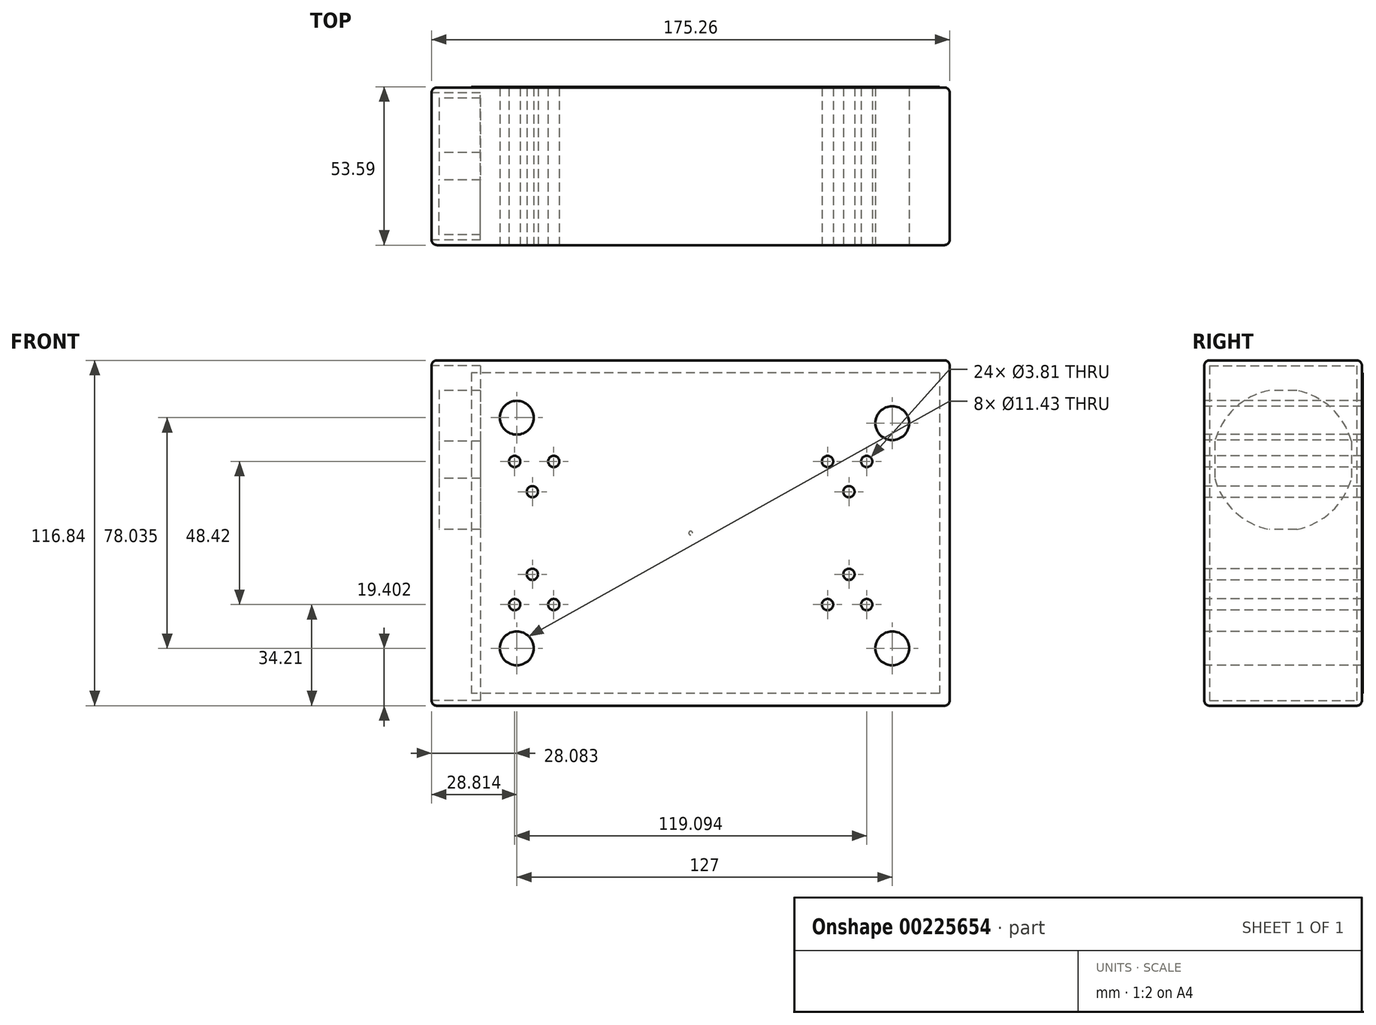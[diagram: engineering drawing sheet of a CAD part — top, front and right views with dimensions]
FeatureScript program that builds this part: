
annotation { "Feature Type Name" : "Feature", "Feature Type Description" : "" }
export const myFeature = defineFeature(function(context is Context, id is Id, definition is map)
    precondition{}
    {
        {
            var Q0;
            Q0=qCreatedBy(makeId("Front.planeOp"),FACE);
            var sketch = newSketch(context, id + "F0", { "sketchPlane" : qUnion([Q0])});
            skLineSegment(sketch, "E0.bottom", {"start": v(-87.63, 58.42) * mm, "end": v(87.63, 58.42) * mm});
            skLineSegment(sketch, "E0.top", {"start": v(-87.63, -58.42) * mm, "end": v(87.63, -58.42) * mm});
            skLineSegment(sketch, "E0.left", {"start": v(-87.63, 58.42) * mm, "end": v(-87.63, -58.42) * mm});
            skLineSegment(sketch, "E0.right", {"start": v(87.63, 58.42) * mm, "end": v(87.63, -58.42) * mm});
            skPoint(sketch, "E0.middle", {"position": v(0, 0) * mm});
            skSolve(sketch);
        }
        {
            var Q0;
            Q0=makeQuery(id+"F0.imprint","IMPRINT",FACE,{"disambiguationData":[TD([[makeQuery(id+"F0.imprint","IMPRINT",EDGE,{"derivedFrom":sQuery(id+"F0.wireOp",EDGE,"E0.bottom")}),-1.0]])]});
            extrude(context, id + "F1", {"entities" : qUnion([Q0]), "depth" : 53.34 * mm});
        }
        {
            var Q0;
            Q0=makeQuery(id+"F1.opExtrude","CAP_FACE",FACE,{"disambiguationData":[OSD([sQuery(id+"F0.wireOp",EDGE,"E0.bottom"),sQuery(id+"F0.wireOp",EDGE,"E0.top"),sQuery(id+"F0.wireOp",EDGE,"E0.left"),sQuery(id+"F0.wireOp",EDGE,"E0.right")])],"isStart":true});
            var sketch = newSketch(context, id + "F2", { "sketchPlane" : qUnion([Q0])});
            skLineSegment(sketch, "E1", {"start": v(-87.63, 54.2) * mm, "end": v(87.63, 54.2) * mm});
            skLineSegment(sketch, "E2.MirrorCS", {"start": v(-87.63, -54.2) * mm, "end": v(87.63, -54.2) * mm});
            skLineSegment(sketch, "E3", {"start": v(74.22, 58.42) * mm, "end": v(74.22, -58.42) * mm});
            skLineSegment(sketch, "E4", {"start": v(-84.2, 54.2) * mm, "end": v(-84.2, -58.42) * mm});
            skCircle(sketch, "E5", {"center": v(0, 0) * mm, "radius": 0.64 * mm});
            skSolve(sketch);
        }
        {
            var Q0;
            Q0 = qSketchRegion(id + "F2", true);
            extrude(context, id + "F3", {"entities" : qUnion([Q0]), "depth" : 0.25 * mm});
        }
        {
            var Q0;
            Q0=makeQuery(id+"F1.opExtrude","CAP_FACE",FACE,{"disambiguationData":[OSD([sQuery(id+"F0.wireOp",EDGE,"E0.bottom"),sQuery(id+"F0.wireOp",EDGE,"E0.top"),sQuery(id+"F0.wireOp",EDGE,"E0.left"),sQuery(id+"F0.wireOp",EDGE,"E0.right")])],"isStart":false});
            var sketch = newSketch(context, id + "F4", { "sketchPlane" : qUnion([Q0])});
            skCircle(sketch, "E6", {"center": v(68.18, -39.02) * mm, "radius": 4.35 * mm});
            skCircle(sketch, "E7", {"center": v(-58.82, -39.02) * mm, "radius": 4.87 * mm});
            skCircle(sketch, "E8", {"center": v(68.18, 37.18) * mm, "radius": 4.37 * mm});
            skCircle(sketch, "E9.MirrorC", {"center": v(-58.82, 39.02) * mm, "radius": 4.87 * mm});
            skCircle(sketch, "E10", {"center": v(59.55, -24.2) * mm, "radius": 1.93 * mm});
            skCircle(sketch, "E11", {"center": v(53.53, -13.98) * mm, "radius": 1.7 * mm});
            skCircle(sketch, "E12", {"center": v(46.31, -24.2) * mm, "radius": 1.93 * mm});
            skCircle(sketch, "E13.MirrorC", {"center": v(59.55, 24.2) * mm, "radius": 1.93 * mm});
            skCircle(sketch, "E14.MirrorC", {"center": v(46.31, 24.2) * mm, "radius": 1.93 * mm});
            skCircle(sketch, "E15.MirrorC", {"center": v(53.53, 13.98) * mm, "radius": 1.7 * mm});
            skCircle(sketch, "E16.MirrorC", {"center": v(-46.31, -24.2) * mm, "radius": 1.93 * mm});
            skCircle(sketch, "E17.MirrorC", {"center": v(-59.55, -24.2) * mm, "radius": 1.93 * mm});
            skCircle(sketch, "E18.MirrorC", {"center": v(-53.53, -13.98) * mm, "radius": 1.7 * mm});
            skCircle(sketch, "E19.MirrorC", {"center": v(-46.31, 24.2) * mm, "radius": 1.93 * mm});
            skCircle(sketch, "E20.MirrorC", {"center": v(-53.53, 13.98) * mm, "radius": 1.7 * mm});
            skCircle(sketch, "E21.MirrorC", {"center": v(-59.55, 24.2) * mm, "radius": 1.93 * mm});
            skSolve(sketch);
        }
        {
            var Q0;
            Q0=sQuery(id+"F4.wireOp",VERTEX,"E6.center");
            var Q1;
            Q1=sQuery(id+"F4.wireOp",VERTEX,"E8.center");
            var Q2;
            Q2=sQuery(id+"F4.wireOp",VERTEX,"E7.center");
            var Q3;
            Q3=sQuery(id+"F4.wireOp",VERTEX,"E9.MirrorC.center");
            var Q4;
            Q4=makeQuery(id+"F1.opExtrude","SWEPT_BODY",BODY,{"disambiguationData":[OSD([sQuery(id+"F0.wireOp",EDGE,"E0.bottom"),sQuery(id+"F0.wireOp",EDGE,"E0.top"),sQuery(id+"F0.wireOp",EDGE,"E0.left"),sQuery(id+"F0.wireOp",EDGE,"E0.right")])]});
            var Q5;
            Q5=makeQuery(id+"F3.opExtrude","SWEPT_BODY",BODY,{"disambiguationData":[OSD([sQuery(id+"F2.wireOp",EDGE,"E1"),sQuery(id+"F2.wireOp",EDGE,"E2.MirrorCS"),sQuery(id+"F2.wireOp",EDGE,"E3"),sQuery(id+"F2.wireOp",EDGE,"E4")])]});
            hole(context, id + "F5", {"style" : HoleStyle.SIMPLE, "endStyle" : HoleEndStyle.BLIND_IN_LAST, "holeDiameter" : 11.43 * mm, "tapDrillDiameter" : 11.43 * mm, "holeDepth" : 12.7 * mm, "locations" : qUnion([Q0, Q1, Q2, Q3]), "scope" : qUnion([Q4, Q5])});
        }
        {
            var Q0;
            Q0=sQuery(id+"F4.wireOp",VERTEX,"E10.center");
            var Q1;
            Q1=sQuery(id+"F4.wireOp",VERTEX,"E11.center");
            var Q2;
            Q2=sQuery(id+"F4.wireOp",VERTEX,"E12.center");
            var Q3;
            Q3=sQuery(id+"F4.wireOp",VERTEX,"E15.MirrorC.center");
            var Q4;
            Q4=sQuery(id+"F4.wireOp",VERTEX,"E14.MirrorC.center");
            var Q5;
            Q5=sQuery(id+"F4.wireOp",VERTEX,"E13.MirrorC.center");
            var Q6;
            Q6=sQuery(id+"F4.wireOp",VERTEX,"E18.MirrorC.center");
            var Q7;
            Q7=sQuery(id+"F4.wireOp",VERTEX,"E17.MirrorC.center");
            var Q8;
            Q8=sQuery(id+"F4.wireOp",VERTEX,"E16.MirrorC.center");
            var Q9;
            Q9=sQuery(id+"F4.wireOp",VERTEX,"E20.MirrorC.center");
            var Q10;
            Q10=sQuery(id+"F4.wireOp",VERTEX,"E21.MirrorC.center");
            var Q11;
            Q11=sQuery(id+"F4.wireOp",VERTEX,"E19.MirrorC.center");
            var Q12;
            Q12=makeQuery(id+"F1.opExtrude","SWEPT_BODY",BODY,{"disambiguationData":[OSD([sQuery(id+"F0.wireOp",EDGE,"E0.bottom"),sQuery(id+"F0.wireOp",EDGE,"E0.top"),sQuery(id+"F0.wireOp",EDGE,"E0.left"),sQuery(id+"F0.wireOp",EDGE,"E0.right")])]});
            var Q13;
            Q13=makeQuery(id+"F3.opExtrude","SWEPT_BODY",BODY,{"disambiguationData":[OSD([sQuery(id+"F2.wireOp",EDGE,"E1"),sQuery(id+"F2.wireOp",EDGE,"E2.MirrorCS"),sQuery(id+"F2.wireOp",EDGE,"E3"),sQuery(id+"F2.wireOp",EDGE,"E4")])]});
            hole(context, id + "F6", {"style" : HoleStyle.SIMPLE, "endStyle" : HoleEndStyle.BLIND_IN_LAST, "holeDiameter" : 3.8 * mm, "tapDrillDiameter" : 3.8 * mm, "holeDepth" : 12.7 * mm, "locations" : qUnion([Q0, Q1, Q2, Q3, Q4, Q5, Q6, Q7, Q8, Q9, Q10, Q11]), "scope" : qUnion([Q12, Q13])});
        }
        {
            var Q0;
            Q0=makeQuery(id+"F1.opExtrude","SWEPT_FACE",FACE,{"disambiguationData":[OSD([sQuery(id+"F0.wireOp",EDGE,"E0.left")])]});
            var Q1;
            Q1=makeQuery(id+"F1.opExtrude","SWEPT_FACE",FACE,{"disambiguationData":[OSD([sQuery(id+"F0.wireOp",EDGE,"E0.bottom")])]});
            var Q2;
            Q2=makeQuery(id+"F1.opExtrude","SWEPT_FACE",FACE,{"disambiguationData":[OSD([sQuery(id+"F0.wireOp",EDGE,"E0.right")])]});
            var Q3;
            Q3=makeQuery(id+"F1.opExtrude","SWEPT_FACE",FACE,{"disambiguationData":[OSD([sQuery(id+"F0.wireOp",EDGE,"E0.top")])]});
            fillet(context, id + "F7", {"entities" : qUnion([Q0, Q1, Q2, Q3]), "radius" : 1.78 * mm, "tangentPropagation" : true, "allowEdgeOverflow" : false});
        }
        {
            var Q0;
            Q0=makeQuery(id+"F1.opExtrude","SWEPT_FACE",FACE,{"disambiguationData":[OSD([sQuery(id+"F0.wireOp",EDGE,"E0.left")])]});
            var sketch = newSketch(context, id + "F8", { "sketchPlane" : qUnion([Q0])});
            skLineSegment(sketch, "E22", {"start": v(1.78, 0) * mm, "end": v(51.56, 0) * mm, "construction": true});
            skLineSegment(sketch, "E23", {"start": v(26.67, -56.64) * mm, "end": v(26.67, 56.64) * mm, "construction": true});
            skPoint(sketch, "E24.middle", {"position": v(26.67, -29.91) * mm});
            skArc(sketch, "E25", {"start": v(31.33, -48.24) * mm, "mid": v(43.02, -42.25) * mm, "end": v(49.79, -31.01) * mm});
            skLineSegment(sketch, "E26.bottom", {"start": v(22, -48.24) * mm, "end": v(31.33, -48.24) * mm});
            skLineSegment(sketch, "E26.top", {"start": v(22, -1.25) * mm, "end": v(31.33, -1.25) * mm});
            skLineSegment(sketch, "E26.left", {"start": v(3.55, -31.01) * mm, "end": v(3.55, -18.48) * mm});
            skLineSegment(sketch, "E26.right", {"start": v(49.79, -31.01) * mm, "end": v(49.79, -18.48) * mm});
            skPoint(sketch, "E27.orphan", {"position": v(3.55, -48.24) * mm});
            skPoint(sketch, "E28.orphan", {"position": v(49.79, -48.24) * mm});
            skArc(sketch, "E29.trimOffspring", {"start": v(3.55, -31.01) * mm, "mid": v(10.32, -42.25) * mm, "end": v(22, -48.24) * mm});
            skPoint(sketch, "E30.orphan", {"position": v(3.55, -1.25) * mm});
            skArc(sketch, "E31.trimOffspring", {"start": v(22, -1.25) * mm, "mid": v(10.32, -7.23) * mm, "end": v(3.55, -18.48) * mm});
            skPoint(sketch, "E32.orphan", {"position": v(49.79, -1.25) * mm});
            skArc(sketch, "E33.trimOffspring", {"start": v(49.79, -18.48) * mm, "mid": v(43.02, -7.23) * mm, "end": v(31.33, -1.25) * mm});
            skArc(sketch, "E34.MirrorCS", {"start": v(22, 1.25) * mm, "mid": v(10.32, 7.23) * mm, "end": v(3.55, 18.48) * mm});
            skLineSegment(sketch, "E35.MirrorCS", {"start": v(22, 1.25) * mm, "end": v(31.33, 1.25) * mm});
            skArc(sketch, "E36.MirrorCS", {"start": v(49.79, 18.48) * mm, "mid": v(43.02, 7.23) * mm, "end": v(31.33, 1.25) * mm});
            skLineSegment(sketch, "E37.MirrorCS", {"start": v(49.79, 31.01) * mm, "end": v(49.79, 18.48) * mm});
            skArc(sketch, "E38.MirrorCS", {"start": v(31.33, 48.24) * mm, "mid": v(43.02, 42.25) * mm, "end": v(49.79, 31.01) * mm});
            skLineSegment(sketch, "E39.MirrorCS", {"start": v(22, 48.24) * mm, "end": v(31.33, 48.24) * mm});
            skArc(sketch, "E40.MirrorCS", {"start": v(3.55, 31.01) * mm, "mid": v(10.32, 42.25) * mm, "end": v(22, 48.24) * mm});
            skLineSegment(sketch, "E41.MirrorCS", {"start": v(3.55, 31.01) * mm, "end": v(3.55, 18.48) * mm});
            skSolve(sketch);
        }
        {
            var Q0;
            Q0=makeQuery(id+"F8.imprint","IMPRINT",FACE,{"disambiguationData":[TD([[makeQuery(id+"F8.imprint","IMPRINT",EDGE,{"derivedFrom":sQuery(id+"F8.wireOp",EDGE,"E25")}),1.0]])]});
            var Q1;
            Q1=makeQuery(id+"F8.imprint","IMPRINT",FACE,{"disambiguationData":[TD([[makeQuery(id+"F8.imprint","IMPRINT",EDGE,{"derivedFrom":sQuery(id+"F8.wireOp",EDGE,"E34.MirrorCS")}),-1.0]])]});
            extrude(context, id + "F9", {"entities" : qUnion([Q0, Q1]), "operationType" : NewBodyOperationType.REMOVE, "oppositeDirection" : true, "depth" : 16.5 * mm});
        }
        {
            var Q0;
            Q0=makeQuery(id+"F1.opExtrude","SWEPT_FACE",FACE,{"disambiguationData":[OSD([sQuery(id+"F0.wireOp",EDGE,"E0.left")])]});
            var sketch = newSketch(context, id + "F10", { "sketchPlane" : qUnion([Q0])});
            skCircle(sketch, "E42", {"center": v(8.88, -51.96) * mm, "radius": 3.43 * mm});
            skLineSegment(sketch, "E43.0", {"start": v(7.32, -51.96) * mm, "end": v(8.1, -50.6) * mm});
            skLineSegment(sketch, "E43.1", {"start": v(8.1, -50.6) * mm, "end": v(9.74, -50.57) * mm});
            skLineSegment(sketch, "E43.2", {"start": v(9.74, -50.57) * mm, "end": v(10.52, -51.92) * mm});
            skLineSegment(sketch, "E43.3", {"start": v(10.52, -51.92) * mm, "end": v(9.67, -53.32) * mm});
            skLineSegment(sketch, "E43.4", {"start": v(9.67, -53.32) * mm, "end": v(8.1, -53.32) * mm});
            skLineSegment(sketch, "E43.5", {"start": v(8.1, -53.32) * mm, "end": v(7.32, -51.96) * mm});
            skLineSegment(sketch, "E44", {"start": v(1.78, 0) * mm, "end": v(51.56, 0) * mm, "construction": true});
            skLineSegment(sketch, "E45", {"start": v(26.67, -56.64) * mm, "end": v(26.67, 56.64) * mm, "construction": true});
            skLineSegment(sketch, "E46.MirrorCS", {"start": v(9.67, 53.32) * mm, "end": v(8.1, 53.32) * mm});
            skLineSegment(sketch, "E47.MirrorCS", {"start": v(8.1, 53.32) * mm, "end": v(7.32, 51.96) * mm});
            skLineSegment(sketch, "E48.MirrorCS", {"start": v(9.74, 50.57) * mm, "end": v(10.52, 51.92) * mm});
            skLineSegment(sketch, "E49.MirrorCS", {"start": v(10.52, 51.92) * mm, "end": v(9.67, 53.32) * mm});
            skLineSegment(sketch, "E50.MirrorCS", {"start": v(8.1, 50.6) * mm, "end": v(9.74, 50.57) * mm});
            skLineSegment(sketch, "E51.MirrorCS", {"start": v(7.32, 51.96) * mm, "end": v(8.1, 50.6) * mm});
            skCircle(sketch, "E52.MirrorC", {"center": v(8.88, 51.96) * mm, "radius": 3.43 * mm});
            skLineSegment(sketch, "E53.MirrorCS", {"start": v(46.02, -51.96) * mm, "end": v(45.24, -50.6) * mm});
            skLineSegment(sketch, "E54.MirrorCS", {"start": v(45.24, -50.6) * mm, "end": v(43.6, -50.57) * mm});
            skLineSegment(sketch, "E55.MirrorCS", {"start": v(45.24, -53.32) * mm, "end": v(46.02, -51.96) * mm});
            skLineSegment(sketch, "E56.MirrorCS", {"start": v(42.82, -51.92) * mm, "end": v(43.67, -53.32) * mm});
            skLineSegment(sketch, "E57.MirrorCS", {"start": v(43.6, -50.57) * mm, "end": v(42.82, -51.92) * mm});
            skLineSegment(sketch, "E58.MirrorCS", {"start": v(43.67, -53.32) * mm, "end": v(45.24, -53.32) * mm});
            skCircle(sketch, "E59.MirrorC", {"center": v(44.46, -51.96) * mm, "radius": 3.43 * mm});
            skLineSegment(sketch, "E60.MirrorCS", {"start": v(46.02, 51.96) * mm, "end": v(45.24, 50.6) * mm});
            skLineSegment(sketch, "E61.MirrorCS", {"start": v(45.24, 53.32) * mm, "end": v(46.02, 51.96) * mm});
            skCircle(sketch, "E62.MirrorC", {"center": v(44.46, 51.96) * mm, "radius": 3.43 * mm});
            skLineSegment(sketch, "E63.MirrorCS", {"start": v(45.24, 50.6) * mm, "end": v(43.6, 50.57) * mm});
            skLineSegment(sketch, "E64.MirrorCS", {"start": v(43.6, 50.57) * mm, "end": v(42.82, 51.92) * mm});
            skLineSegment(sketch, "E65.MirrorCS", {"start": v(42.82, 51.92) * mm, "end": v(43.67, 53.32) * mm});
            skLineSegment(sketch, "E66.MirrorCS", {"start": v(43.67, 53.32) * mm, "end": v(45.24, 53.32) * mm});
            skSolve(sketch);
        }
        {
            var Q0;
            Q0=makeQuery(id+"F10.imprint","IMPRINT",FACE,{"disambiguationData":[TD([[makeQuery(id+"F10.imprint","IMPRINT",EDGE,{"derivedFrom":sQuery(id+"F10.wireOp",EDGE,"E42")}),1.0]])]});
            var Q1;
            Q1=makeQuery(id+"F10.imprint","IMPRINT",FACE,{"disambiguationData":[TD([[makeQuery(id+"F10.imprint","IMPRINT",EDGE,{"derivedFrom":sQuery(id+"F10.wireOp",EDGE,"E53.MirrorCS")}),-1.0]])]});
            var Q2;
            Q2=makeQuery(id+"F10.imprint","IMPRINT",FACE,{"disambiguationData":[TD([[makeQuery(id+"F10.imprint","IMPRINT",EDGE,{"derivedFrom":sQuery(id+"F10.wireOp",EDGE,"E60.MirrorCS")}),1.0]])]});
            var Q3;
            Q3=makeQuery(id+"F10.imprint","IMPRINT",FACE,{"disambiguationData":[TD([[makeQuery(id+"F10.imprint","IMPRINT",EDGE,{"derivedFrom":sQuery(id+"F10.wireOp",EDGE,"E46.MirrorCS")}),-1.0]])]});
            var Q4;
            Q4=sQuery(id+"F10.wireOp",EDGE,"E42");
            var Q5;
            Q5=sQuery(id+"F10.wireOp",EDGE,"E52.MirrorC");
            var Q6;
            Q6=sQuery(id+"F10.wireOp",EDGE,"E62.MirrorC");
            var Q7;
            Q7=sQuery(id+"F10.wireOp",EDGE,"E59.MirrorC");
            extrude(context, id + "F11", {"entities" : qUnion([Q0, Q1, Q2, Q3]), "operationType" : NewBodyOperationType.REMOVE, "surfaceEntities" : qUnion([Q4, Q5, Q6, Q7]), "oppositeDirection" : true, "depth" : 1.02 * mm});
        }
        {
            var Q0;
            Q0=makeQuery(id+"F11.boolean.opBoolean","SPLIT",FACE,{"disambiguationData":[TD([makeQuery(id+"F11.opExtrude","SWEPT_FACE",FACE,{"disambiguationData":[OSD([sQuery(id+"F10.wireOp",EDGE,"E43.0")])]})])],"derivedFrom":makeQuery(id+"F1.opExtrude","SWEPT_FACE",FACE,{"disambiguationData":[OSD([sQuery(id+"F0.wireOp",EDGE,"E0.left")])]})});
            var Q1;
            Q1=makeQuery(id+"F11.boolean.opBoolean","SPLIT",FACE,{"disambiguationData":[TD([makeQuery(id+"F11.opExtrude","SWEPT_FACE",FACE,{"disambiguationData":[OSD([sQuery(id+"F10.wireOp",EDGE,"E53.MirrorCS")])]})])],"derivedFrom":makeQuery(id+"F1.opExtrude","SWEPT_FACE",FACE,{"disambiguationData":[OSD([sQuery(id+"F0.wireOp",EDGE,"E0.left")])]})});
            var Q2;
            Q2=makeQuery(id+"F11.boolean.opBoolean","SPLIT",FACE,{"disambiguationData":[TD([makeQuery(id+"F11.opExtrude","SWEPT_FACE",FACE,{"disambiguationData":[OSD([sQuery(id+"F10.wireOp",EDGE,"E46.MirrorCS")])]})])],"derivedFrom":makeQuery(id+"F1.opExtrude","SWEPT_FACE",FACE,{"disambiguationData":[OSD([sQuery(id+"F0.wireOp",EDGE,"E0.left")])]})});
            var Q3;
            Q3=makeQuery(id+"F11.boolean.opBoolean","SPLIT",FACE,{"disambiguationData":[TD([makeQuery(id+"F11.opExtrude","SWEPT_FACE",FACE,{"disambiguationData":[OSD([sQuery(id+"F10.wireOp",EDGE,"E60.MirrorCS")])]})])],"derivedFrom":makeQuery(id+"F1.opExtrude","SWEPT_FACE",FACE,{"disambiguationData":[OSD([sQuery(id+"F0.wireOp",EDGE,"E0.left")])]})});
            extrude(context, id + "F12", {"entities" : qUnion([Q0, Q1, Q2, Q3]), "operationType" : NewBodyOperationType.REMOVE, "oppositeDirection" : true, "depth" : 2.54 * mm});
        }
        {
            var Q0;
            Q0=makeQuery(id+"F3.opExtrude","SWEPT_BODY",BODY,{"disambiguationData":[OSD([sQuery(id+"F2.wireOp",EDGE,"E1"),sQuery(id+"F2.wireOp",EDGE,"E2.MirrorCS"),sQuery(id+"F2.wireOp",EDGE,"E3"),sQuery(id+"F2.wireOp",EDGE,"E4"),sQuery(id+"F2.wireOp",EDGE,"E5")])]});
            transform(context, id + "F13", {"entities" : qUnion([Q0]), "transformType" : TransformType.TRANSLATION_3D, "dx" : 0 * mm, "dy" : 0 * mm, "dz" : 0 * mm, "makeCopy" : true});
        }
        {
            var Q0;
            Q0=makeQuery(id+"F13.opPattern","COPY",BODY,{"derivedFrom":makeQuery(id+"F3.opExtrude","SWEPT_BODY",BODY,{"disambiguationData":[OSD([sQuery(id+"F2.wireOp",EDGE,"E1"),sQuery(id+"F2.wireOp",EDGE,"E2.MirrorCS"),sQuery(id+"F2.wireOp",EDGE,"E3"),sQuery(id+"F2.wireOp",EDGE,"E4"),sQuery(id+"F2.wireOp",EDGE,"E5")])]}),"instanceName":"1"});
            deleteBodies(context, id + "F14", {"entities" : qUnion([Q0])});
        }
    });
